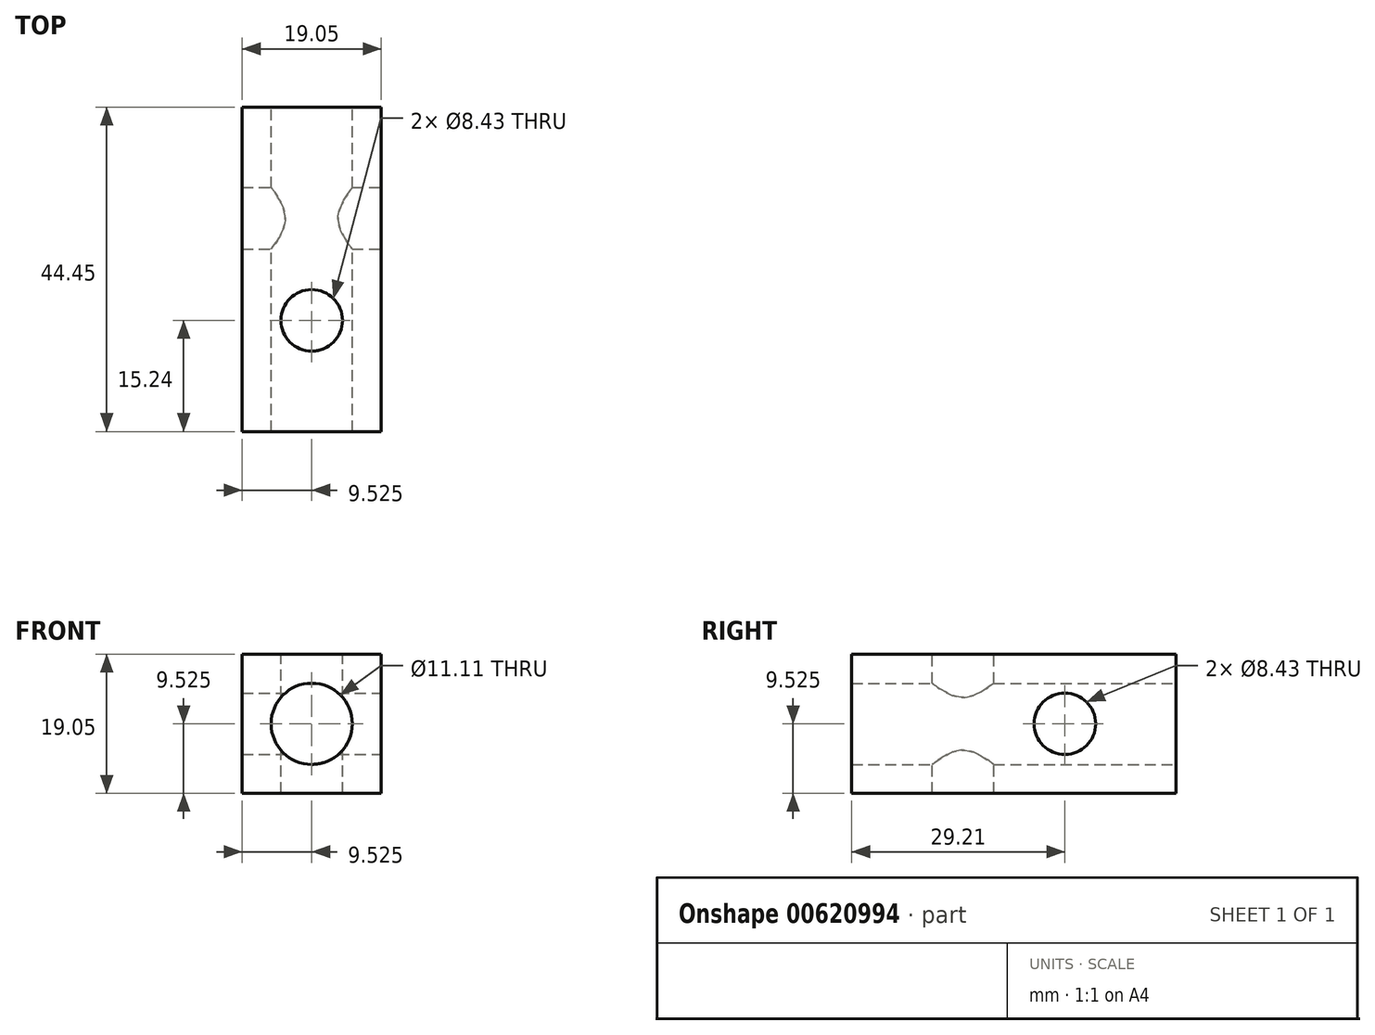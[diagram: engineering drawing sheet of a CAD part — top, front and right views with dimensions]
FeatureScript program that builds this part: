
annotation { "Feature Type Name" : "Feature", "Feature Type Description" : "" }
export const myFeature = defineFeature(function(context is Context, id is Id, definition is map)
    precondition{}
    {
        {
            var Q0;
            Q0=qCreatedBy(makeId("Front.planeOp"),FACE);
            var sketch = newSketch(context, id + "F0", { "sketchPlane" : qUnion([Q0])});
            skLineSegment(sketch, "E0.bottom", {"start": v(0, 0) * mm, "end": v(19.05, 0) * mm});
            skLineSegment(sketch, "E0.top", {"start": v(0, 19.05) * mm, "end": v(19.05, 19.05) * mm});
            skLineSegment(sketch, "E0.left", {"start": v(0, 0) * mm, "end": v(0, 19.05) * mm});
            skLineSegment(sketch, "E0.right", {"start": v(19.05, 0) * mm, "end": v(19.05, 19.05) * mm});
            skCircle(sketch, "E1", {"center": v(9.53, 9.52) * mm, "radius": 5.56 * mm});
            skPoint(sketch, "E1.centerSnap0", {"position": v(19.05, 9.53) * mm});
            skSolve(sketch);
        }
        {
            var Q0;
            Q0 = qSketchRegion(id + "F0", true);
            extrude(context, id + "F1", {"entities" : qUnion([Q0]), "depth" : 44.45 * mm, "offsetDistance" : 25.4 * mm});
        }
        {
            var Q0;
            Q0=makeQuery(id+"F1.opExtrude","SWEPT_FACE",FACE,{"disambiguationData":[OSD([sQuery(id+"F0.wireOp",EDGE,"E0.top")])]});
            var sketch = newSketch(context, id + "F2", { "sketchPlane" : qUnion([Q0])});
            skPoint(sketch, "E2", {"position": v(9.53, -29.21) * mm});
            skSolve(sketch);
        }
        {
            var Q0;
            Q0=sQuery(id+"F2.wireOp",VERTEX,"1255a1d2-045f-4a7d-8120-8c63db4c7ace");
            var Q1;
            Q1=sQuery(id+"F2.wireOp",VERTEX,"E2");
            var Q2;
            Q2=makeQuery(id+"F1.opExtrude","SWEPT_BODY",BODY,{"disambiguationData":[OSD([sQuery(id+"F0.wireOp",EDGE,"E0.bottom"),sQuery(id+"F0.wireOp",EDGE,"E0.top"),sQuery(id+"F0.wireOp",EDGE,"E0.left"),sQuery(id+"F0.wireOp",EDGE,"E0.right"),sQuery(id+"F0.wireOp",EDGE,"E1")])]});
            hole(context, id + "F3", {"style" : HoleStyle.SIMPLE, "endStyle" : HoleEndStyle.THROUGH, "holeDiameter" : 8.43 * mm, "majorDiameter" : 6.35 * mm, "isTappedThrough" : true, "tappedDepth" : 12.7 * mm, "tapClearance" : 3, "startFromSketch" : true, "locations" : qUnion([Q0, Q1]), "scope" : qUnion([Q2])});
        }
        {
            var Q0;
            Q0=makeQuery(id+"F1.opExtrude","SWEPT_FACE",FACE,{"disambiguationData":[OSD([sQuery(id+"F0.wireOp",EDGE,"E0.right")])]});
            var sketch = newSketch(context, id + "F4", { "sketchPlane" : qUnion([Q0])});
            skPoint(sketch, "E3", {"position": v(-15.24, 9.53) * mm});
            skPoint(sketch, "E3.positionSnap0", {"position": v(0, 9.53) * mm});
            skSolve(sketch);
        }
        {
            var Q0;
            Q0=sQuery(id+"F4.wireOp",VERTEX,"E3");
            var Q1;
            Q1=makeQuery(id+"F1.opExtrude","SWEPT_BODY",BODY,{"disambiguationData":[OSD([sQuery(id+"F0.wireOp",EDGE,"E0.bottom"),sQuery(id+"F0.wireOp",EDGE,"E0.top"),sQuery(id+"F0.wireOp",EDGE,"E0.left"),sQuery(id+"F0.wireOp",EDGE,"E0.right"),sQuery(id+"F0.wireOp",EDGE,"E1")])]});
            hole(context, id + "F5", {"style" : HoleStyle.SIMPLE, "endStyle" : HoleEndStyle.THROUGH, "holeDiameter" : 8.43 * mm, "majorDiameter" : 6.35 * mm, "isTappedThrough" : true, "tappedDepth" : 12.7 * mm, "tapClearance" : 3, "startFromSketch" : true, "locations" : qUnion([Q0]), "scope" : qUnion([Q1])});
        }
    });
